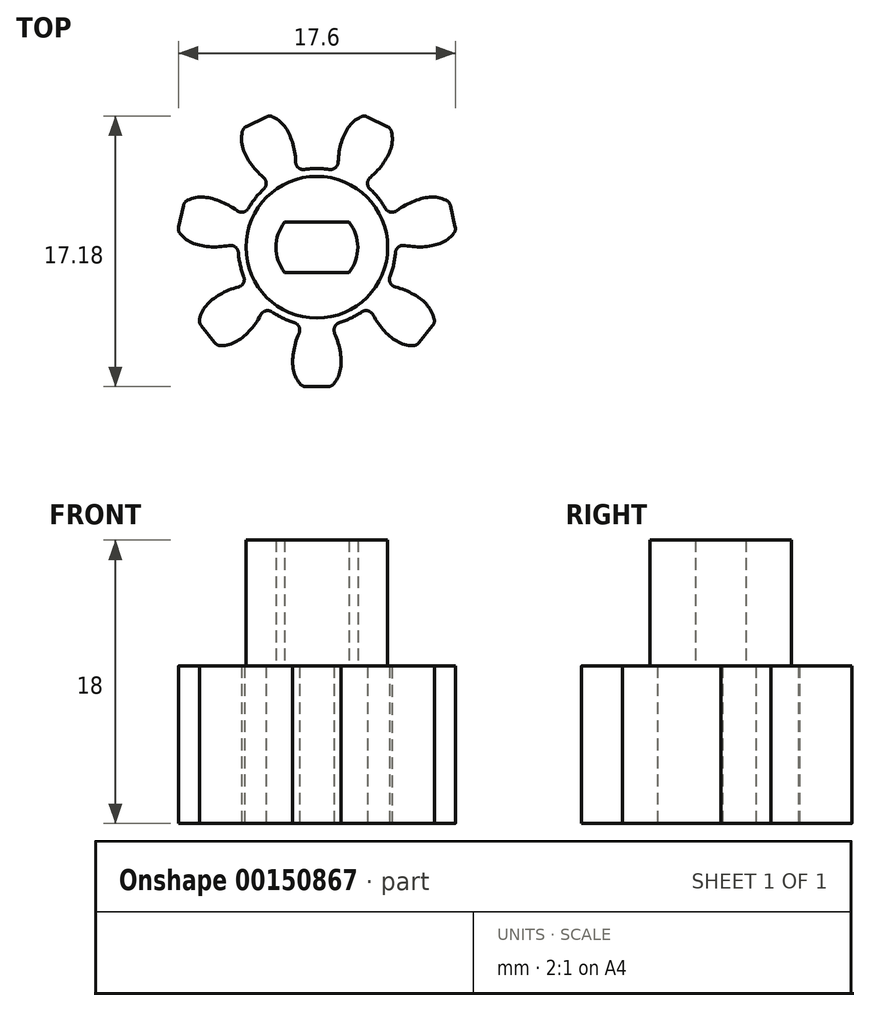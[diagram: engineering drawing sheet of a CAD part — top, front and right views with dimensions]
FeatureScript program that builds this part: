
annotation { "Feature Type Name" : "Feature", "Feature Type Description" : "" }
export const myFeature = defineFeature(function(context is Context, id is Id, definition is map)
    precondition{}
    {
        {
            var Q0;
            Q0=qCreatedBy(makeId("Top.planeOp"),FACE);
            var sketch = newSketch(context, id + "F0", { "sketchPlane" : qUnion([Q0])});
            skCircle(sketch, "E0", {"center": v(0, 0) * mm, "radius": 7 * mm, "construction": true});
            skLineSegment(sketch, "E1", {"start": v(0, -8.29) * mm, "end": v(0, 8.45) * mm, "construction": true});
            skLineSegment(sketch, "E2", {"start": v(0, 0) * mm, "end": v(2.17, -4.5) * mm});
            skLineSegment(sketch, "E3", {"start": v(0, 0) * mm, "end": v(-2.17, -4.5) * mm});
            skArc(sketch, "E4", {"start": v(-2.17, -4.5) * mm, "mid": v(-1.81, -4.66) * mm, "end": v(-1.45, -4.79) * mm});
            skLineSegment(sketch, "E5", {"start": v(-0.7, -8.85) * mm, "end": v(0.7, -8.85) * mm});
            skPoint(sketch, "E6", {"position": v(0, -8.85) * mm});
            skFitSpline(sketch, "E7", {"points": [v(-0.91, -8.85) * mm, v(-1.54, -7.23) * mm, v(-0.85, -4.93) * mm], "startDerivative": vector(-3.06, 3) * mm, "endDerivative": vector(2.45, 3.97) * mm});
            skFitSpline(sketch, "E8.MirrorCS", {"points": [v(0.91, -8.85) * mm, v(1.54, -7.23) * mm, v(0.85, -4.93) * mm], "startDerivative": vector(3.06, 3) * mm, "endDerivative": vector(-2.45, 3.97) * mm});
            skArc(sketch, "E9.MirrorCS", {"start": v(2.17, -4.5) * mm, "mid": v(1.81, -4.66) * mm, "end": v(1.45, -4.79) * mm});
            skArc(sketch, "E10.filletArc", {"start": v(-1.13, -5.47) * mm, "mid": v(-1.14, -5.06) * mm, "end": v(-1.45, -4.79) * mm});
            skArc(sketch, "E11.filletArc", {"start": v(1.45, -4.79) * mm, "mid": v(1.14, -5.06) * mm, "end": v(1.13, -5.47) * mm});
            skArc(sketch, "E12.filletArc", {"start": v(0.7, -8.85) * mm, "mid": v(0.9, -8.8) * mm, "end": v(1.08, -8.67) * mm});
            skArc(sketch, "E13.filletArc", {"start": v(-1.08, -8.67) * mm, "mid": v(-0.9, -8.8) * mm, "end": v(-0.7, -8.85) * mm});
            skSolve(sketch);
        }
        {
            var Q0;
            Q0=makeQuery(id+"F0.imprint","IMPRINT",FACE,{"disambiguationData":[TD([[makeQuery(id+"F0.imprint","IMPRINT",EDGE,{"derivedFrom":sQuery(id+"F0.wireOp",EDGE,"E2")}),-1.0]])]});
            extrude(context, id + "F1", {"entities" : qUnion([Q0]), "depth" : 10 * mm});
        }
        {
            var Q0;
            Q0=makeQuery(id+"F1.opExtrude","SWEPT_BODY",BODY,{"disambiguationData":[OSD([sQuery(id+"F0.wireOp",EDGE,"E2"),sQuery(id+"F0.wireOp",EDGE,"E3"),sQuery(id+"F0.wireOp",EDGE,"E4"),sQuery(id+"F0.wireOp",EDGE,"E5"),sQuery(id+"F0.wireOp",EDGE,"E7"),sQuery(id+"F0.wireOp",EDGE,"E8.MirrorCS"),sQuery(id+"F0.wireOp",EDGE,"E9.MirrorCS"),sQuery(id+"F0.wireOp",EDGE,"E10.filletArc"),sQuery(id+"F0.wireOp",EDGE,"E11.filletArc"),sQuery(id+"F0.wireOp",EDGE,"E12.filletArc"),sQuery(id+"F0.wireOp",EDGE,"E13.filletArc")])]});
            var Q1;
            Q1=makeQuery(id+"F1.opExtrude","SWEPT_EDGE",EDGE,{"disambiguationData":[OSD([sQuery(id+"F0.wireOp",EDGE,"E2"),sQuery(id+"F0.wireOp",EDGE,"E3")])]});
            circularPattern(context, id + "F2", {"operationType" : NewBodyOperationType.ADD, "entities" : qUnion([Q0]), "axis" : qUnion([Q1]), "angle" : 51.43 * degree, "instanceCount" : 7});
        }
        {
            var Q0;
            {var subQ0=makeQuery(id+"F1.opExtrude","CAP_FACE",FACE,{"disambiguationData":[OSD([sQuery(id+"F0.wireOp",EDGE,"E2"),sQuery(id+"F0.wireOp",EDGE,"E3"),sQuery(id+"F0.wireOp",EDGE,"E4"),sQuery(id+"F0.wireOp",EDGE,"E5"),sQuery(id+"F0.wireOp",EDGE,"E7"),sQuery(id+"F0.wireOp",EDGE,"E8.MirrorCS"),sQuery(id+"F0.wireOp",EDGE,"E9.MirrorCS"),sQuery(id+"F0.wireOp",EDGE,"E10.filletArc"),sQuery(id+"F0.wireOp",EDGE,"E11.filletArc"),sQuery(id+"F0.wireOp",EDGE,"E12.filletArc"),sQuery(id+"F0.wireOp",EDGE,"E13.filletArc")])],"isStart":false});Q0=makeQuery(id+"F2.boolean.opBoolean","MERGE",FACE,{"derivedFrom":[subQ0,makeQuery(id+"F2.opPattern","COPY",FACE,{"derivedFrom":subQ0,"instanceName":"1"}),makeQuery(id+"F2.opPattern","COPY",FACE,{"derivedFrom":subQ0,"instanceName":"2"}),makeQuery(id+"F2.opPattern","COPY",FACE,{"derivedFrom":subQ0,"instanceName":"3"}),makeQuery(id+"F2.opPattern","COPY",FACE,{"derivedFrom":subQ0,"instanceName":"4"}),makeQuery(id+"F2.opPattern","COPY",FACE,{"derivedFrom":subQ0,"instanceName":"5"}),makeQuery(id+"F2.opPattern","COPY",FACE,{"derivedFrom":subQ0,"instanceName":"6"})]});}
            var sketch = newSketch(context, id + "F3", { "sketchPlane" : qUnion([Q0])});
            skCircle(sketch, "E14", {"center": v(0, 0) * mm, "radius": 4.5 * mm});
            skCircle(sketch, "E15", {"center": v(0, 0) * mm, "radius": 2.6 * mm});
            skLineSegment(sketch, "E16", {"start": v(-2.05, 1.6) * mm, "end": v(2.05, 1.6) * mm});
            skLineSegment(sketch, "E17", {"start": v(-2.05, -1.6) * mm, "end": v(2.05, -1.6) * mm});
            skSolve(sketch);
        }
        {
            var Q0;
            Q0=makeQuery(id+"F3.imprint","IMPRINT",FACE,{"disambiguationData":[TD([[makeQuery(id+"F3.imprint","IMPRINT",EDGE,{"derivedFrom":sQuery(id+"F3.wireOp",EDGE,"E14")}),1.0]])]});
            var Q1;
            {var subQ0=sQuery(id+"F3.wireOp",EDGE,"E16");Q1=makeQuery(id+"F3.imprint","IMPRINT",FACE,{"disambiguationData":[TD([[makeQuery(id+"F3.imprint","IMPRINT",EDGE,{"derivedFrom":subQ0}),1.0]])]});}
            var Q2;
            {var subQ0=sQuery(id+"F3.wireOp",EDGE,"E17");Q2=makeQuery(id+"F3.imprint","IMPRINT",FACE,{"disambiguationData":[TD([[makeQuery(id+"F3.imprint","IMPRINT",EDGE,{"derivedFrom":subQ0}),-1.0]])]});}
            extrude(context, id + "F4", {"entities" : qUnion([Q0, Q1, Q2]), "operationType" : NewBodyOperationType.ADD, "depth" : 8 * mm});
        }
    });
